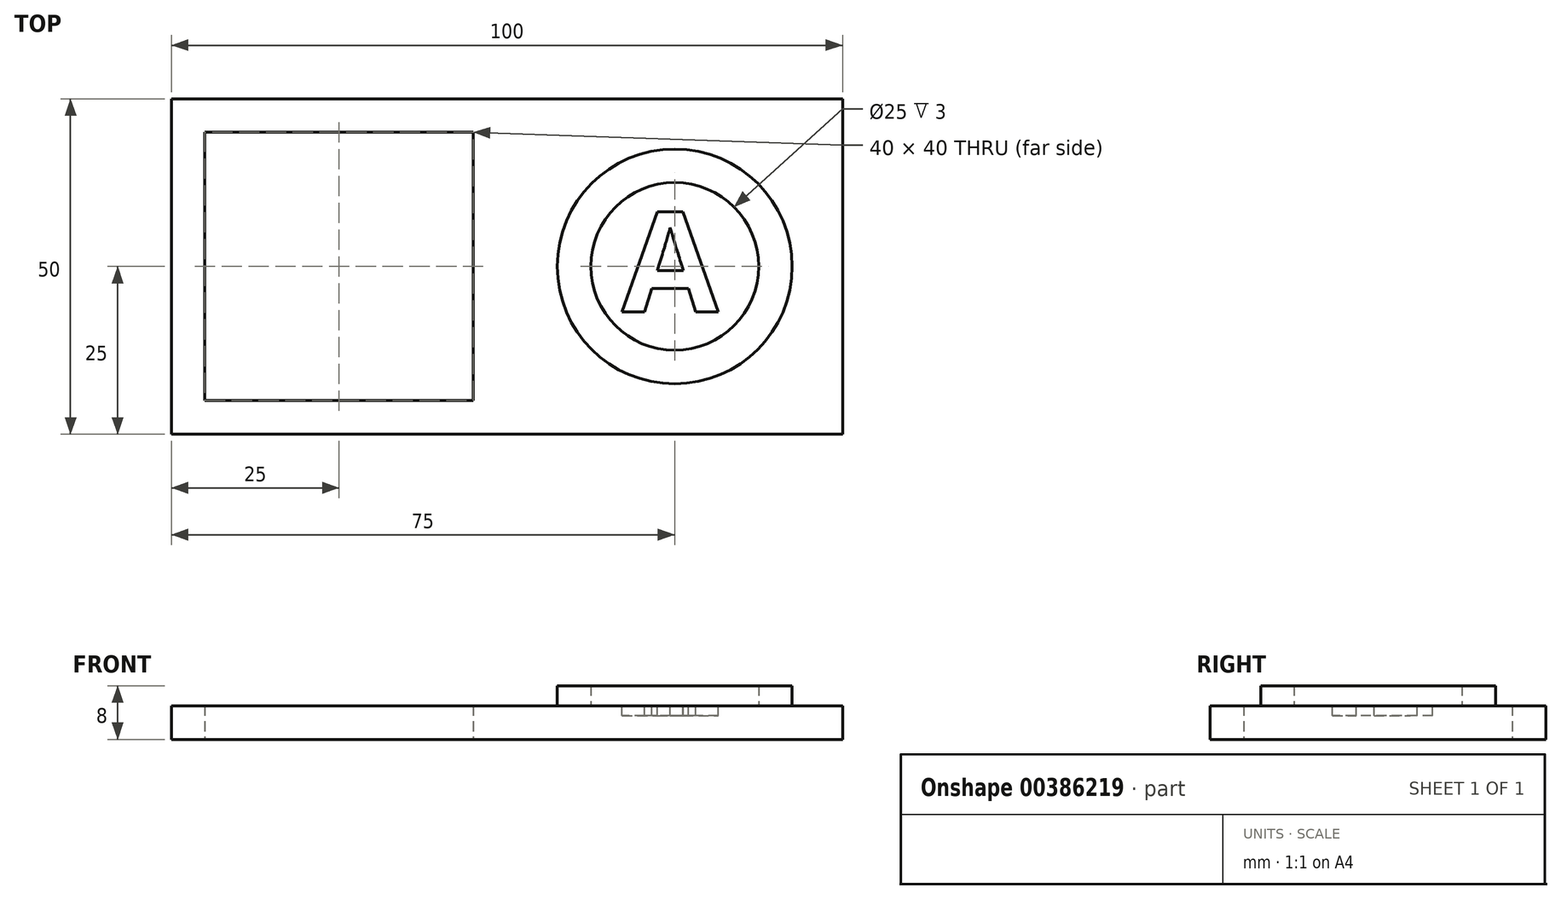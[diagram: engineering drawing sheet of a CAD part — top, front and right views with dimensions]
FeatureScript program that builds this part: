
annotation { "Feature Type Name" : "Feature", "Feature Type Description" : "" }
export const myFeature = defineFeature(function(context is Context, id is Id, definition is map)
    precondition{}
    {
        {
            var Q0;
            Q0=qCreatedBy(makeId("Top.planeOp"),FACE);
            var sketch = newSketch(context, id + "F0", { "sketchPlane" : qUnion([Q0])});
            skLineSegment(sketch, "E0.bottom", {"start": v(50, -25) * mm, "end": v(-50, -25) * mm});
            skLineSegment(sketch, "E0.top", {"start": v(50, 25) * mm, "end": v(-50, 25) * mm});
            skLineSegment(sketch, "E0.left", {"start": v(50, -25) * mm, "end": v(50, 25) * mm});
            skLineSegment(sketch, "E0.right", {"start": v(-50, -25) * mm, "end": v(-50, 25) * mm});
            skPoint(sketch, "E0.middle", {"position": v(0, 0) * mm});
            skLineSegment(sketch, "E1.bottom", {"start": v(-5, -20) * mm, "end": v(-45, -20) * mm});
            skLineSegment(sketch, "E1.top", {"start": v(-5, 20) * mm, "end": v(-45, 20) * mm});
            skLineSegment(sketch, "E1.left", {"start": v(-5, -20) * mm, "end": v(-5, 20) * mm});
            skLineSegment(sketch, "E1.right", {"start": v(-45, -20) * mm, "end": v(-45, 20) * mm});
            skPoint(sketch, "E1.middle", {"position": v(-25, 0) * mm});
            skSolve(sketch);
        }
        {
            var Q0;
            Q0 = qSketchRegion(id + "F0", true);
            extrude(context, id + "F1", {"entities" : qUnion([Q0]), "depth" : 5 * mm});
        }
        {
            var Q0;
            Q0=makeQuery(id+"F1.opExtrude","CAP_FACE",FACE,{"disambiguationData":[OSD([sQuery(id+"F0.wireOp",EDGE,"E0.bottom"),sQuery(id+"F0.wireOp",EDGE,"E0.top"),sQuery(id+"F0.wireOp",EDGE,"E0.left"),sQuery(id+"F0.wireOp",EDGE,"E0.right"),sQuery(id+"F0.wireOp",EDGE,"E1.bottom"),sQuery(id+"F0.wireOp",EDGE,"E1.top"),sQuery(id+"F0.wireOp",EDGE,"E1.left"),sQuery(id+"F0.wireOp",EDGE,"E1.right")])],"isStart":false});
            var sketch = newSketch(context, id + "F2", { "sketchPlane" : qUnion([Q0])});
            skCircle(sketch, "E2", {"center": v(25, 0) * mm, "radius": 17.5 * mm});
            skCircle(sketch, "E3", {"center": v(25, 0) * mm, "radius": 12.5 * mm});
            skSolve(sketch);
        }
        {
            var Q0;
            Q0 = qSketchRegion(id + "F2", true);
            extrude(context, id + "F3", {"entities" : qUnion([Q0]), "operationType" : NewBodyOperationType.ADD, "depth" : 3 * mm});
        }
        {
            var Q0;
            Q0=makeQuery(id+"F3.boolean.opBoolean","SPLIT",FACE,{"disambiguationData":[TD([makeQuery(id+"F3.opExtrude","SWEPT_FACE",FACE,{"disambiguationData":[OSD([sQuery(id+"F2.wireOp",EDGE,"E3")])]})])],"derivedFrom":makeQuery(id+"F1.opExtrude","CAP_FACE",FACE,{"disambiguationData":[OSD([sQuery(id+"F0.wireOp",EDGE,"E0.bottom"),sQuery(id+"F0.wireOp",EDGE,"E0.top"),sQuery(id+"F0.wireOp",EDGE,"E0.left"),sQuery(id+"F0.wireOp",EDGE,"E0.right"),sQuery(id+"F0.wireOp",EDGE,"E1.bottom"),sQuery(id+"F0.wireOp",EDGE,"E1.top"),sQuery(id+"F0.wireOp",EDGE,"E1.left"),sQuery(id+"F0.wireOp",EDGE,"E1.right")])],"isStart":false})});
            var sketch = newSketch(context, id + "F4", { "sketchPlane" : qUnion([Q0])});
            skText(sketch, "E4", { "text": "A", "fontName": "OpenSans-Bold.ttf"});
            const initialGuessF4  = {"E4": [0.01714, -0.0068, 1, 0, 0.015]};
            skSetInitialGuess(sketch, initialGuessF4);
            skSolve(sketch);
        }
        {
            var Q0;
            Q0 = qSketchRegion(id + "F4", true);
            extrude(context, id + "F5", {"entities" : qUnion([Q0]), "operationType" : NewBodyOperationType.REMOVE, "oppositeDirection" : true, "depth" : 1.5 * mm});
        }
    });
